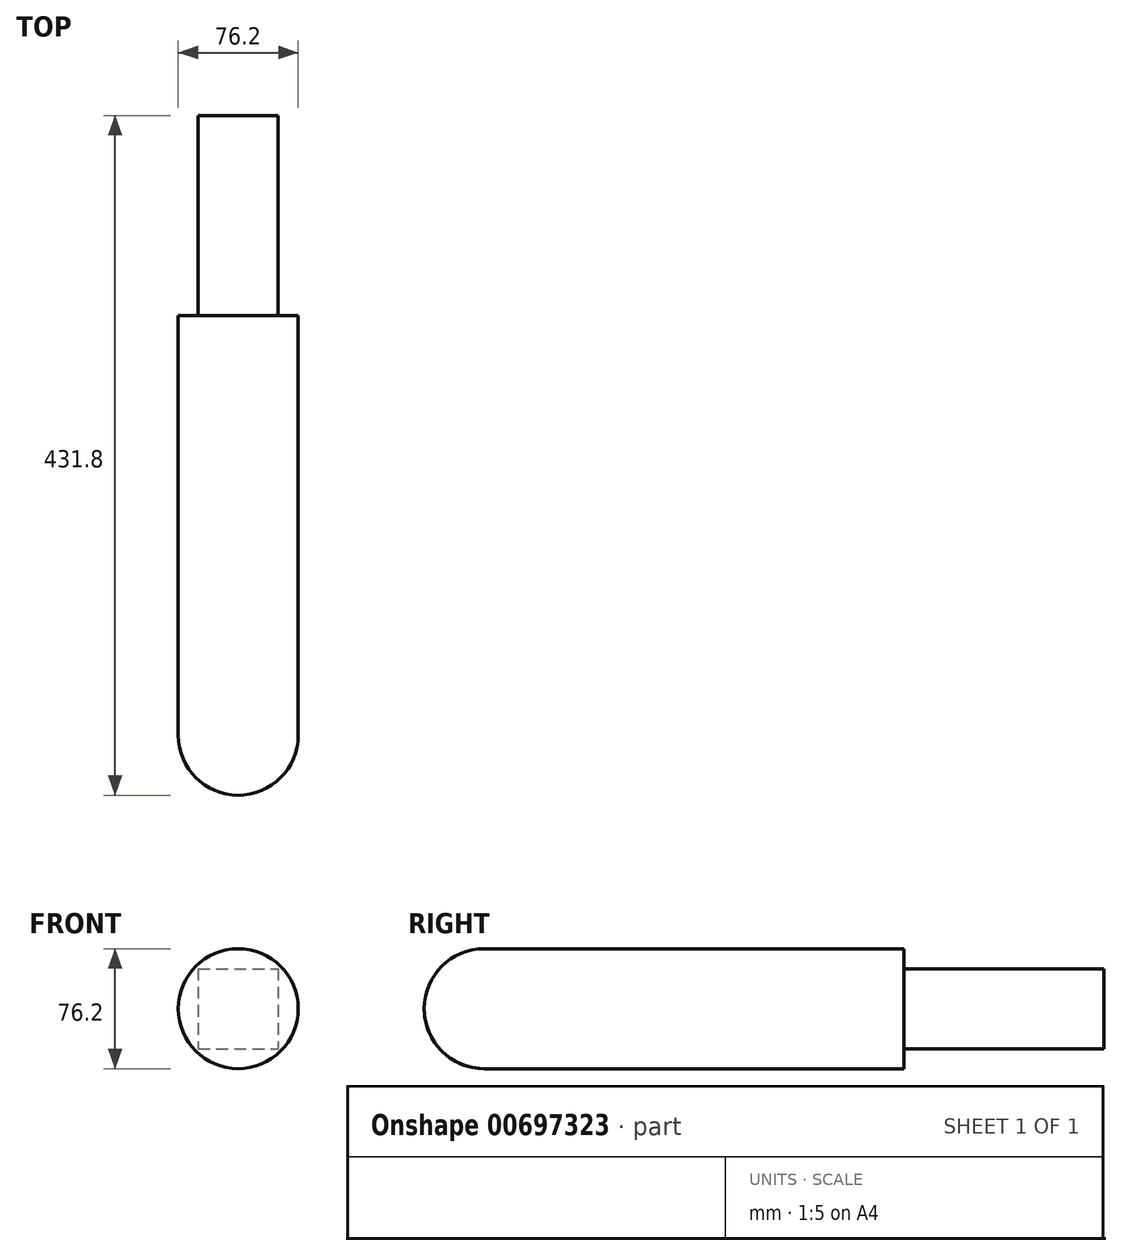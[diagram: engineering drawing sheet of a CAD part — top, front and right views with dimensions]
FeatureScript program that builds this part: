
annotation { "Feature Type Name" : "Feature", "Feature Type Description" : "" }
export const myFeature = defineFeature(function(context is Context, id is Id, definition is map)
    precondition{}
    {
        {
            var Q0;
            Q0=qCreatedBy(makeId("Front.planeOp"),FACE);
            var sketch = newSketch(context, id + "F0", { "sketchPlane" : qUnion([Q0])});
            skLineSegment(sketch, "E0.bottom", {"start": v(-25.4, 25.4) * mm, "end": v(25.4, 25.4) * mm});
            skLineSegment(sketch, "E0.top", {"start": v(-25.4, -25.4) * mm, "end": v(25.4, -25.4) * mm});
            skLineSegment(sketch, "E0.left", {"start": v(-25.4, 25.4) * mm, "end": v(-25.4, -25.4) * mm});
            skLineSegment(sketch, "E0.right", {"start": v(25.4, 25.4) * mm, "end": v(25.4, -25.4) * mm});
            skPoint(sketch, "E0.middle", {"position": v(0, 0) * mm});
            skSolve(sketch);
        }
        {
            var Q0;
            Q0 = qSketchRegion(id + "F0", true);
            extrude(context, id + "F1", {"entities" : qUnion([Q0]), "depth" : 25.4 * mm, "offsetDistance" : 25.4 * mm});
        }
        {
            var Q0;
            Q0=makeQuery(id+"F1.opExtrude","CAP_FACE",FACE,{"disambiguationData":[OSD([sQuery(id+"F0.wireOp",EDGE,"E0.bottom"),sQuery(id+"F0.wireOp",EDGE,"E0.top"),sQuery(id+"F0.wireOp",EDGE,"E0.left"),sQuery(id+"F0.wireOp",EDGE,"E0.right")])],"isStart":false});
            extrude(context, id + "F2", {"entities" : qUnion([Q0]), "operationType" : NewBodyOperationType.ADD, "depth" : 101.6 * mm, "offsetDistance" : 25.4 * mm});
        }
        {
            var Q0;
            Q0=makeQuery(id+"F2.opExtrude","CAP_FACE",FACE,{"disambiguationData":[OSD([sQuery(id+"F0.wireOp",EDGE,"E0.bottom"),sQuery(id+"F0.wireOp",EDGE,"E0.top"),sQuery(id+"F0.wireOp",EDGE,"E0.left"),sQuery(id+"F0.wireOp",EDGE,"E0.right")])],"isStart":false});
            var sketch = newSketch(context, id + "F3", { "sketchPlane" : qUnion([Q0])});
            skCircle(sketch, "E1", {"center": v(0, 0) * mm, "radius": 38.1 * mm});
            skSolve(sketch);
        }
        {
            var Q0;
            Q0 = qSketchRegion(id + "F3", true);
            extrude(context, id + "F4", {"entities" : qUnion([Q0]), "operationType" : NewBodyOperationType.ADD, "depth" : 304.8 * mm, "offsetDistance" : 25.4 * mm});
        }
        {
            var Q0;
            Q0=makeQuery(id+"F4.opExtrude","CAP_FACE",FACE,{"disambiguationData":[OSD([sQuery(id+"F3.wireOp",EDGE,"E1")])],"isStart":false});
            fillet(context, id + "F5", {"entities" : qUnion([Q0]), "radius" : 38.1 * mm, "tangentPropagation" : true, "allowEdgeOverflow" : false});
        }
    });
